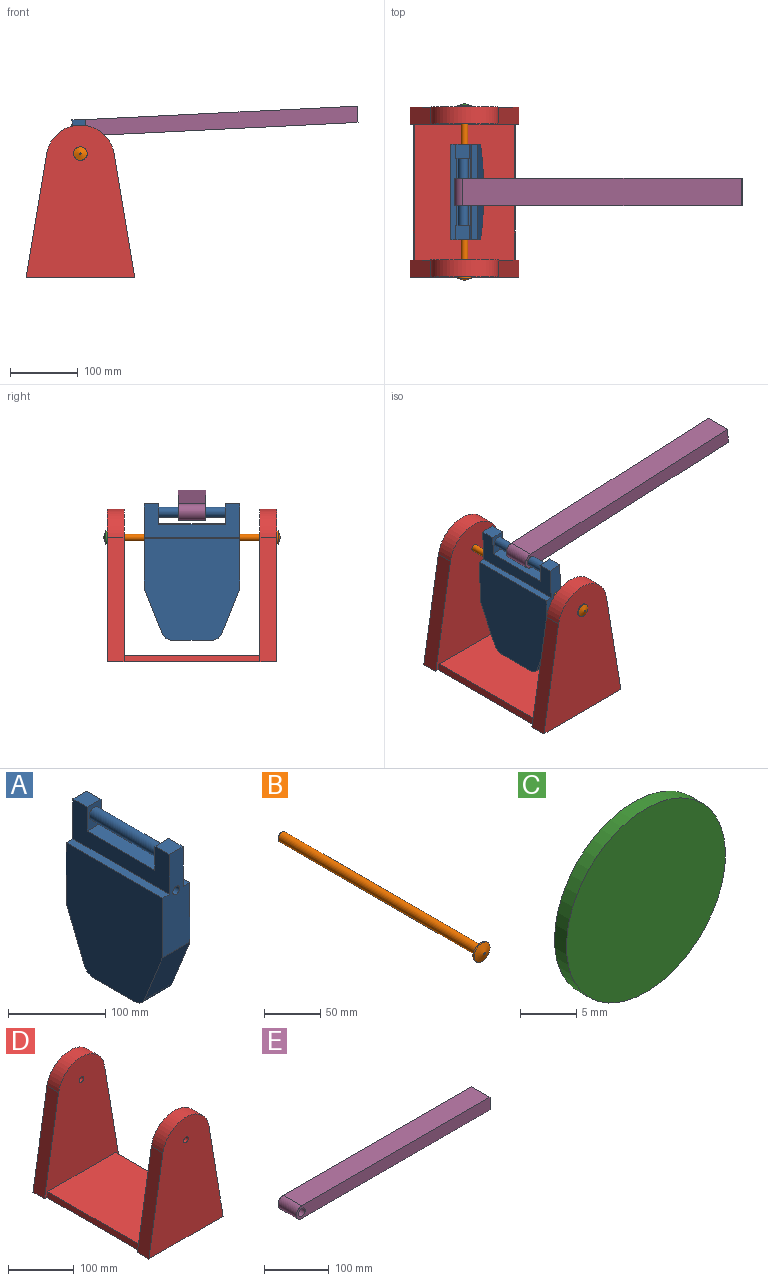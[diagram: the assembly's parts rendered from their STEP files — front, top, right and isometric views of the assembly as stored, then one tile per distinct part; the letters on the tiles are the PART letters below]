
ASSEMBLY  parts=5 mates=4
PART A: 20 faces, bbox 40x140x200 mm
  f0: plane 125x40mm, normal (0,-1,0), area 3921.5mm2, adj f2,f4,f6,f7,f8,f9,f10,f11
  f1: plane 125x40mm, normal (0,1,0), area 3921.5mm2, adj f2,f4,f5,f6,f7,f9,f10,f11
  f2: plane 150x140mm, normal (-1,0,0), area 18713.2mm2, adj f0,f1,f3,f10,f16,f17,f18,f19
  f3: plane 59.69x40mm, normal (0,0,-1), area 2387.6mm2, adj f2,f4,f17,f19
  f4: plane 150x140mm, normal (1,0,0), area 18713.2mm2, adj f0,f1,f3,f6,f16,f17,f18,f19
  f5: plane 20.79x20mm, normal (0,0,1), area 415.8mm2, adj f1,f7,f9,f12
  f6: plane 140x10mm, normal (0,0,1), area 1400mm2, adj f0,f1,f4,f7
  f7: plane 140x50mm, normal (1,0,0), area 4047.5mm2, adj f0,f1,f5,f6,f8,f12,f13,f14
  f8: plane 20.79x20mm, normal (0,0,1), area 415.8mm2, adj f0,f7,f9,f13
  f9: plane 140x50mm, normal (-1,0,0), area 4047.5mm2, adj f0,f1,f5,f8,f10,f12,f13,f14
  f10: plane 140x10mm, normal (0,0,1), area 1400mm2, adj f0,f1,f2,f9
  f11: cylinder r=5mm len=140mm, axis (0,1,0), area 4398.2mm2, adj f0,f1
  f12: plane 30x20mm, normal (0,-1,0), area 434.4mm2, adj f5,f7,f9,f14,f15
  f13: plane 30x20mm, normal (0,1,0), area 434.4mm2, adj f7,f8,f9,f14,f15
  f14: plane 98.42x20mm, normal (0,0,1), area 1968.3mm2, adj f7,f9,f12,f13
  f15: cylinder r=7.26mm len=98.42mm, axis (0,1,0), area 4489mm2, adj f12,f13
  f16: plane 65.57x40mm, normal (0,-0.93,-0.37), area 2824.9mm2, adj f0,f2,f4,f17
  f17: cylinder r=15mm len=40mm, axis (1,0,0), area 714.2mm2, adj f2,f3,f4,f16
  f18: plane 65.57x40mm, normal (0,0.93,-0.37), area 2824.9mm2, adj f1,f2,f4,f19
  f19: cylinder r=15mm len=40mm, axis (1,0,0), area 714.2mm2, adj f2,f3,f4,f18
PART B: 6 faces, bbox 20x254.5x20 mm
  f0: cylinder r=10mm len=20mm, axis (0,1,0), area 94.2mm2, adj f1,f3
  f1: plane 20x20mm, normal (0,1,0), area 235.6mm2, adj f0,f4
  f2: plane 2x2mm, normal (0,-1,0), area 3.1mm2, adj f3
  f3: cone r=1mm half-angle=71.6deg, axis (0,1,0), area 327.8mm2, adj f0,f2
  f4: cylinder r=5mm len=250mm, axis (0,1,0), area 7854mm2, adj f1,f5
  f5: plane 10x10mm, normal (0,1,0), area 78.5mm2, adj f4
PART C: 4 faces, bbox 20x4.5x20 mm
  f0: cylinder r=10mm len=20mm, axis (0,-1,0), area 94.2mm2, adj f1,f3
  f1: plane 20x20mm, normal (0,-1,0), area 314.2mm2, adj f0
  f2: plane 2x2mm, normal (0,1,0), area 3.1mm2, adj f3
  f3: cone r=1mm half-angle=71.6deg, axis (0,-1,0), area 327.8mm2, adj f0,f2
PART D: 16 faces, bbox 160x250x224.8 mm
  f0: plane 224.82x160mm, normal (0,1,0), area 25272.5mm2, adj f1,f2,f3,f4,f5,f13,f14,f15
  f1: plane 182.8x30.41mm, normal (0.99,0,0.16), area 4632.9mm2, adj f0,f2,f5,f6
  f2: cylinder r=50.27mm len=99.18mm, axis (0,1,0), area 3533.9mm2, adj f0,f1,f3,f6
  f3: plane 182.8x30.41mm, normal (-0.99,0,0.16), area 4632.9mm2, adj f0,f2,f5,f6
  f4: cylinder r=5mm len=25mm, axis (0,1,0), area 785.4mm2, adj f0,f6
  f5: plane 250x160mm, normal (0,0,-1), area 37972.5mm2, adj f0,f1,f3,f6,f7,f9,f11,f12
  f6: plane 224.82x160mm, normal (0,-1,0), area 26754.5mm2, adj f1,f2,f3,f4,f5
  f7: plane 182.8x30.41mm, normal (0.99,0,0.16), area 4632.9mm2, adj f5,f8,f11,f12
  f8: cylinder r=50.27mm len=99.18mm, axis (0,1,0), area 3533.9mm2, adj f7,f9,f11,f12
  f9: plane 182.8x30.41mm, normal (-0.99,0,0.16), area 4632.9mm2, adj f5,f8,f11,f12
  f10: cylinder r=5mm len=25mm, axis (0,1,0), area 785.4mm2, adj f11,f12
  f11: plane 224.82x160mm, normal (0,-1,0), area 25272.5mm2, adj f5,f7,f8,f9,f10,f13,f14,f15
  f12: plane 224.82x160mm, normal (0,1,0), area 26754.5mm2, adj f5,f7,f8,f9,f10
  f13: plane 200x10mm, normal (0.99,0,0.16), area 2027.5mm2, adj f0,f5,f11,f14
  f14: plane 200x146.54mm, normal (0,0,1), area 29307.1mm2, adj f0,f11,f13,f15
  f15: plane 200x10mm, normal (-0.99,0,0.16), area 2027.5mm2, adj f0,f5,f11,f14
PART E: 7 faces, bbox 422x40x24 mm
  f0: plane 410x40mm, normal (0,0,1), area 16400mm2, adj f1,f4,f5,f6
  f1: cylinder r=12mm len=40mm, axis (0,1,0), area 1508mm2, adj f0,f2,f4,f5
  f2: plane 410x40mm, normal (0,0,-1), area 16400mm2, adj f1,f4,f5,f6
  f3: cylinder r=7.26mm len=40mm, axis (0,1,0), area 1824.5mm2, adj f4,f5
  f4: plane 422x24mm, normal (0,-1,0), area 9900.6mm2, adj f0,f1,f2,f3,f6
  f5: plane 422x24mm, normal (0,1,0), area 9900.6mm2, adj f0,f1,f2,f3,f6
  f6: plane 40x24mm, normal (1,0,0), area 960mm2, adj f0,f2,f4,f5
PLACE A rot(axis=(0,-1,0),2.8deg) t=(0,0,0)mm
PLACE B at identity
PLACE C at identity
PLACE D at identity fixed
PLACE E rot(axis=(1,0,0.02),180deg) t=(-3.71,-250.79,74.91)mm
MATE fastened E.f3 <-> A.f15  axis (0,-1,0) through (-1.85,-145,37.45)mm
MATE revolute A.f11 <-> B.f4  axis (0,-1,0) through (0,-195,0)mm
MATE fastened D.f4 <-> C.f0  axis (0,1,0) through (0,0,0)mm
MATE fastened D.f4 <-> B.f4  axis (0,1,0) through (0,0,0)mm
